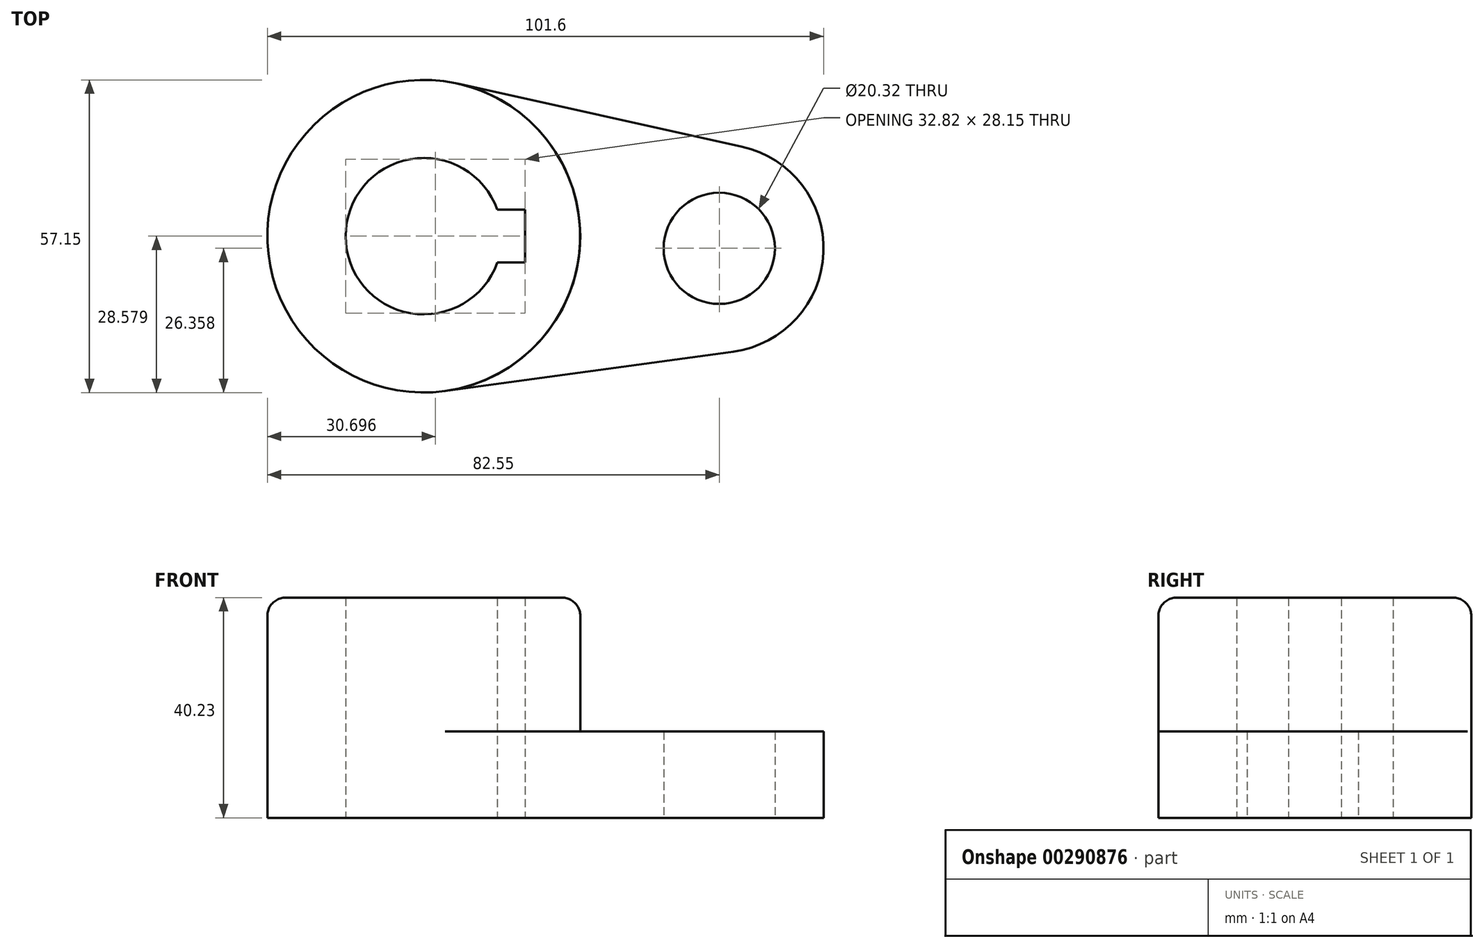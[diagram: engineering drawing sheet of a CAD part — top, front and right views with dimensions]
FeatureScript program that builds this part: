
annotation { "Feature Type Name" : "Feature", "Feature Type Description" : "" }
export const myFeature = defineFeature(function(context is Context, id is Id, definition is map)
    precondition{}
    {
        {
            var Q0;
            Q0=qCreatedBy(makeId("Top.planeOp"),FACE);
            var sketch = newSketch(context, id + "F0", { "sketchPlane" : qUnion([Q0])});
            skCircle(sketch, "E0", {"center": v(-22.74, 6.17) * mm, "radius": 28.57 * mm});
            skCircle(sketch, "E1", {"center": v(31.23, 3.95) * mm, "radius": 10.16 * mm});
            skArc(sketch, "E2", {"start": v(-9.3, 11) * mm, "mid": v(-37.03, 6.17) * mm, "end": v(-9.3, 1.34) * mm});
            skArc(sketch, "E3", {"start": v(33.82, -14.93) * mm, "mid": v(50.26, 3.16) * mm, "end": v(35.36, 22.55) * mm});
            skLineSegment(sketch, "E4", {"start": v(-16.55, 34.07) * mm, "end": v(35.36, 22.55) * mm});
            skLineSegment(sketch, "E5", {"start": v(-18.87, -22.14) * mm, "end": v(33.82, -14.93) * mm});
            skLineSegment(sketch, "E6", {"start": v(-9.3, 11) * mm, "end": v(-4.22, 11) * mm});
            skLineSegment(sketch, "E7", {"start": v(-9.3, 1.34) * mm, "end": v(-4.22, 1.34) * mm});
            skLineSegment(sketch, "E8", {"start": v(-4.22, 11) * mm, "end": v(-4.22, 1.34) * mm});
            skSolve(sketch);
        }
        {
            var Q0;
            Q0=makeQuery(id+"F0.imprint","IMPRINT",FACE,{"disambiguationData":[TD([[makeQuery(id+"F0.imprint","IMPRINT",EDGE,{"derivedFrom":sQuery(id+"F0.wireOp",EDGE,"E2")}),-1.0]])]});
            extrude(context, id + "F1", {"entities" : qUnion([Q0]), "depth" : 40.23 * mm});
        }
        {
            var Q0;
            Q0=makeQuery(id+"F0.imprint","IMPRINT",FACE,{"disambiguationData":[TD([[makeQuery(id+"F0.imprint","IMPRINT",EDGE,{"derivedFrom":sQuery(id+"F0.wireOp",EDGE,"E1")}),-1.0]])]});
            extrude(context, id + "F2", {"entities" : qUnion([Q0]), "operationType" : NewBodyOperationType.ADD, "depth" : 15.77 * mm});
        }
        {
            var Q0;
            Q0=makeQuery(id+"F1.opExtrude","CAP_EDGE",EDGE,{"disambiguationData":[OSD([sQuery(id+"F0.wireOp",EDGE,"E0")])],"isStart":false});
            fillet(context, id + "F3", {"entities" : qUnion([Q0]), "radius" : 3.3 * mm, "tangentPropagation" : true, "allowEdgeOverflow" : false});
        }
    });
